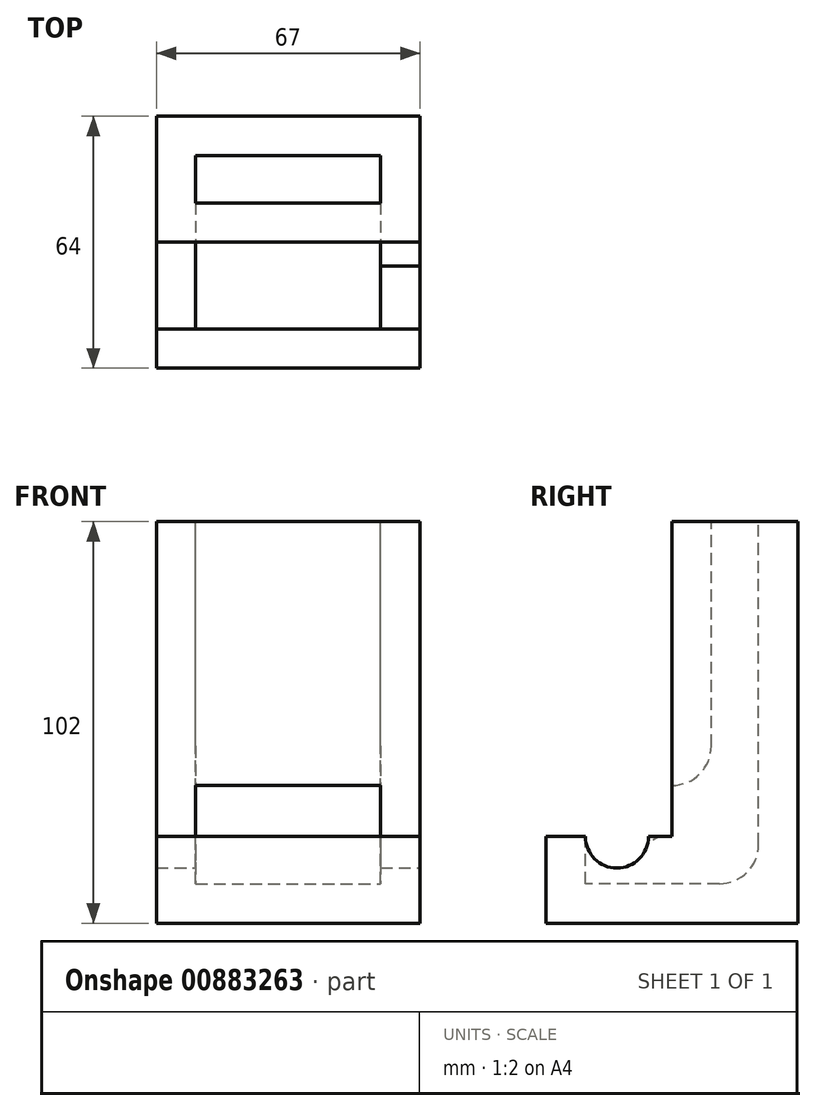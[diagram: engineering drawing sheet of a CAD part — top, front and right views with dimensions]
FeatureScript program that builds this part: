
annotation { "Feature Type Name" : "Feature", "Feature Type Description" : "" }
export const myFeature = defineFeature(function(context is Context, id is Id, definition is map)
    precondition{}
    {
        {
            var Q0;
            Q0=qCreatedBy(makeId("Right.planeOp"),FACE);
            var sketch = newSketch(context, id + "F0", { "sketchPlane" : qUnion([Q0])});
            skLineSegment(sketch, "E0.bottom", {"start": v(0, 0) * mm, "end": v(64, 0) * mm});
            skLineSegment(sketch, "E0.top", {"start": v(0, 22) * mm, "end": v(32, 22) * mm});
            skLineSegment(sketch, "E0.left", {"start": v(0, 0) * mm, "end": v(0, 22) * mm});
            skLineSegment(sketch, "E0.right", {"start": v(64, 0) * mm, "end": v(64, 22) * mm});
            skLineSegment(sketch, "E1.top", {"start": v(64, 102) * mm, "end": v(32, 102) * mm});
            skLineSegment(sketch, "E1.left", {"start": v(64, 22) * mm, "end": v(64, 102) * mm});
            skLineSegment(sketch, "E1.right", {"start": v(32, 22) * mm, "end": v(32, 102) * mm});
            skSolve(sketch);
        }
        {
            var Q0;
            Q0=makeQuery(id+"F0.imprint","IMPRINT",FACE,{"disambiguationData":[TD([[makeQuery(id+"F0.imprint","IMPRINT",EDGE,{"derivedFrom":sQuery(id+"F0.wireOp",EDGE,"E0.bottom")}),1.0]])]});
            extrude(context, id + "F1", {"entities" : qUnion([Q0]), "oppositeDirection" : true, "depth" : 67 * mm, "offsetDistance" : 25 * mm});
        }
        {
            var Q0;
            Q0=makeQuery(id+"F1.opExtrude","SWEPT_FACE",FACE,{"disambiguationData":[OSD([sQuery(id+"F0.wireOp",EDGE,"E1.top")])]});
            var sketch = newSketch(context, id + "F2", { "sketchPlane" : qUnion([Q0])});
            skLineSegment(sketch, "E2.bottom", {"start": v(-57, 54) * mm, "end": v(-10, 54) * mm});
            skLineSegment(sketch, "E2.top", {"start": v(-57, 42) * mm, "end": v(-10, 42) * mm});
            skLineSegment(sketch, "E2.left", {"start": v(-57, 54) * mm, "end": v(-57, 42) * mm});
            skLineSegment(sketch, "E2.right", {"start": v(-10, 54) * mm, "end": v(-10, 42) * mm});
            skSolve(sketch);
        }
        {
            var Q0;
            Q0=makeQuery(id+"F2.imprint","IMPRINT",FACE,{"disambiguationData":[TD([[makeQuery(id+"F2.imprint","IMPRINT",EDGE,{"derivedFrom":sQuery(id+"F2.wireOp",EDGE,"E2.bottom")}),-1.0]])]});
            extrude(context, id + "F3", {"entities" : qUnion([Q0]), "operationType" : NewBodyOperationType.ADD, "oppositeDirection" : true, "depth" : 92 * mm, "offsetDistance" : 25 * mm});
        }
        {
            var Q0;
            Q0 = qSketchRegion(id + "F2", true);
            extrude(context, id + "F4", {"entities" : qUnion([Q0]), "operationType" : NewBodyOperationType.REMOVE, "oppositeDirection" : true, "depth" : 92 * mm, "offsetDistance" : 25 * mm});
        }
        {
            var Q0;
            Q0=makeQuery(id+"F1.opExtrude","SWEPT_FACE",FACE,{"disambiguationData":[OSD([sQuery(id+"F0.wireOp",EDGE,"E0.top")])]});
            var sketch = newSketch(context, id + "F5", { "sketchPlane" : qUnion([Q0])});
            skLineSegment(sketch, "E3.bottom", {"start": v(-57, 10) * mm, "end": v(-10, 10) * mm});
            skLineSegment(sketch, "E3.top", {"start": v(-57, 32) * mm, "end": v(-10, 32) * mm});
            skLineSegment(sketch, "E3.left", {"start": v(-57, 10) * mm, "end": v(-57, 32) * mm});
            skLineSegment(sketch, "E3.right", {"start": v(-10, 10) * mm, "end": v(-10, 32) * mm});
            skSolve(sketch);
        }
        {
            var Q0;
            Q0=makeQuery(id+"F5.imprint","IMPRINT",FACE,{"disambiguationData":[TD([[makeQuery(id+"F5.imprint","IMPRINT",EDGE,{"derivedFrom":sQuery(id+"F5.wireOp",EDGE,"E3.bottom")}),1.0]])]});
            extrude(context, id + "F6", {"entities" : qUnion([Q0]), "operationType" : NewBodyOperationType.REMOVE, "oppositeDirection" : true, "depth" : 12 * mm, "offsetDistance" : 25 * mm});
        }
        {
            var Q0;
            Q0=makeQuery(id+"F6.boolean.opBoolean","MERGE",FACE,{"derivedFrom":[makeQuery(id+"F1.opExtrude","SWEPT_FACE",FACE,{"disambiguationData":[OSD([sQuery(id+"F0.wireOp",EDGE,"E1.right")])]})],"fromTools":[makeQuery(id+"F6.opExtrude","SWEPT_FACE",FACE,{"disambiguationData":[OSD([sQuery(id+"F5.wireOp",EDGE,"E3.top")])]})]});
            var sketch = newSketch(context, id + "F7", { "sketchPlane" : qUnion([Q0])});
            skLineSegment(sketch, "E4.bottom", {"start": v(-57, 10) * mm, "end": v(-10, 10) * mm});
            skLineSegment(sketch, "E4.top", {"start": v(-57, 35) * mm, "end": v(-10, 35) * mm});
            skLineSegment(sketch, "E4.left", {"start": v(-57, 10) * mm, "end": v(-57, 35) * mm});
            skLineSegment(sketch, "E4.right", {"start": v(-10, 10) * mm, "end": v(-10, 35) * mm});
            skSolve(sketch);
        }
        {
            var Q0;
            {var subQ13=sQuery(id+"F7.wireOp",EDGE,"E4.bottom");Q0=makeQuery(id+"F7.imprint","IMPRINT",FACE,{"disambiguationData":[TD([[makeQuery(id+"F7.imprint","IMPRINT",EDGE,{"derivedFrom":subQ13}),1.0]])]});}
            extrude(context, id + "F8", {"entities" : qUnion([Q0]), "operationType" : NewBodyOperationType.REMOVE, "oppositeDirection" : true, "depth" : 22 * mm, "offsetDistance" : 25 * mm});
        }
        {
            var Q0;
            Q0=makeQuery(id+"F4.boolean.opBoolean","COPY",EDGE,{"derivedFrom":makeQuery(id+"F4.opExtrude","CAP_EDGE",EDGE,{"disambiguationData":[OSD([sQuery(id+"F2.wireOp",EDGE,"E2.bottom")])],"isStart":false})});
            var Q1;
            Q1=makeQuery(id+"F8.boolean.opBoolean","INTERSECT",EDGE,{"derivedFrom":[makeQuery(id+"F4.boolean.opBoolean","COPY",FACE,{"derivedFrom":makeQuery(id+"F4.opExtrude","SWEPT_FACE",FACE,{"disambiguationData":[OSD([sQuery(id+"F2.wireOp",EDGE,"E2.top")])]})}),makeQuery(id+"F8.opExtrude","SWEPT_FACE",FACE,{"disambiguationData":[OSD([sQuery(id+"F7.wireOp",EDGE,"E4.top")])]})]});
            fillet(context, id + "F9", {"entities" : qUnion([Q0, Q1]), "radius" : 10 * mm, "tangentPropagation" : true, "allowEdgeOverflow" : false});
        }
        {
            var Q0;
            Q0=makeQuery(id+"F1.opExtrude","CAP_FACE",FACE,{"disambiguationData":[OSD([sQuery(id+"F0.wireOp",EDGE,"E0.bottom"),sQuery(id+"F0.wireOp",EDGE,"E0.top"),sQuery(id+"F0.wireOp",EDGE,"E0.left"),sQuery(id+"F0.wireOp",EDGE,"E0.right"),sQuery(id+"F0.wireOp",EDGE,"E1.top"),sQuery(id+"F0.wireOp",EDGE,"E1.left"),sQuery(id+"F0.wireOp",EDGE,"E1.right")])],"isStart":true});
            var sketch = newSketch(context, id + "F10", { "sketchPlane" : qUnion([Q0])});
            skCircle(sketch, "E5", {"center": v(18, 22) * mm, "radius": 8 * mm});
            skSolve(sketch);
        }
        {
            var Q0;
            {var subQ0=sQuery(id+"F10.wireOp",EDGE,"E5");var subQ1=makeQuery(id+"F1.opExtrude","CAP_EDGE",EDGE,{"disambiguationData":[OSD([sQuery(id+"F0.wireOp",EDGE,"E0.top")])],"isStart":true});var subQ2=makeQuery(id+"F10.imprint","INTERSECT",VERTEX,{"disambiguationData":[OD(0.0)],"derivedFrom":[subQ1,subQ0]});Q0=makeQuery(id+"F10.imprint","IMPRINT",FACE,{"disambiguationData":[TD([[makeQuery(id+"F10.imprint","IMPRINT",EDGE,{"disambiguationData":[TD([[subQ2,-1.0]])],"derivedFrom":subQ0}),1.0]])]});}
            extrude(context, id + "F11", {"entities" : qUnion([Q0]), "operationType" : NewBodyOperationType.REMOVE, "oppositeDirection" : true, "depth" : 83 * mm, "offsetDistance" : 25 * mm});
        }
        {
            var Q0;
            {var subQ0=sQuery(id+"F10.wireOp",EDGE,"E5");var subQ1=sQuery(id+"F0.wireOp",EDGE,"E0.top");Q0=makeQuery(id+"F11.boolean.opBoolean","COPY",EDGE,{"disambiguationData":[TD([makeQuery(id+"F4.boolean.opBoolean","COPY",FACE,{"derivedFrom":makeQuery(id+"F4.opExtrude","SWEPT_FACE",FACE,{"disambiguationData":[OSD([sQuery(id+"F2.wireOp",EDGE,"E2.right")])]})})])],"derivedFrom":makeQuery(id+"F11.opExtrude","SWEPT_EDGE",EDGE,{"disambiguationData":[OSD([subQ1,subQ0]),TDD([makeQuery(id+"F10.imprint","INTERSECT",VERTEX,{"disambiguationData":[OD(1.0)],"derivedFrom":[makeQuery(id+"F1.opExtrude","CAP_EDGE",EDGE,{"disambiguationData":[OSD([subQ1])],"isStart":true}),subQ0]})])]})});}
            var Q1;
            {var subQ0=sQuery(id+"F0.wireOp",EDGE,"E0.top");var subQ1=sQuery(id+"F10.wireOp",EDGE,"E5");Q1=makeQuery(id+"F11.boolean.opBoolean","COPY",EDGE,{"disambiguationData":[TD([makeQuery(id+"F4.boolean.opBoolean","COPY",FACE,{"derivedFrom":makeQuery(id+"F4.opExtrude","SWEPT_FACE",FACE,{"disambiguationData":[OSD([sQuery(id+"F2.wireOp",EDGE,"E2.left")])]})})])],"derivedFrom":makeQuery(id+"F11.opExtrude","SWEPT_EDGE",EDGE,{"disambiguationData":[OSD([subQ0,subQ1]),TDD([makeQuery(id+"F10.imprint","INTERSECT",VERTEX,{"disambiguationData":[OD(1.0)],"derivedFrom":[makeQuery(id+"F1.opExtrude","CAP_EDGE",EDGE,{"disambiguationData":[OSD([subQ0])],"isStart":true}),subQ1]})])]})});}
            fillet(context, id + "F12", {"entities" : qUnion([Q0, Q1]), "radius" : 5 * mm, "tangentPropagation" : true, "allowEdgeOverflow" : false});
        }
    });
